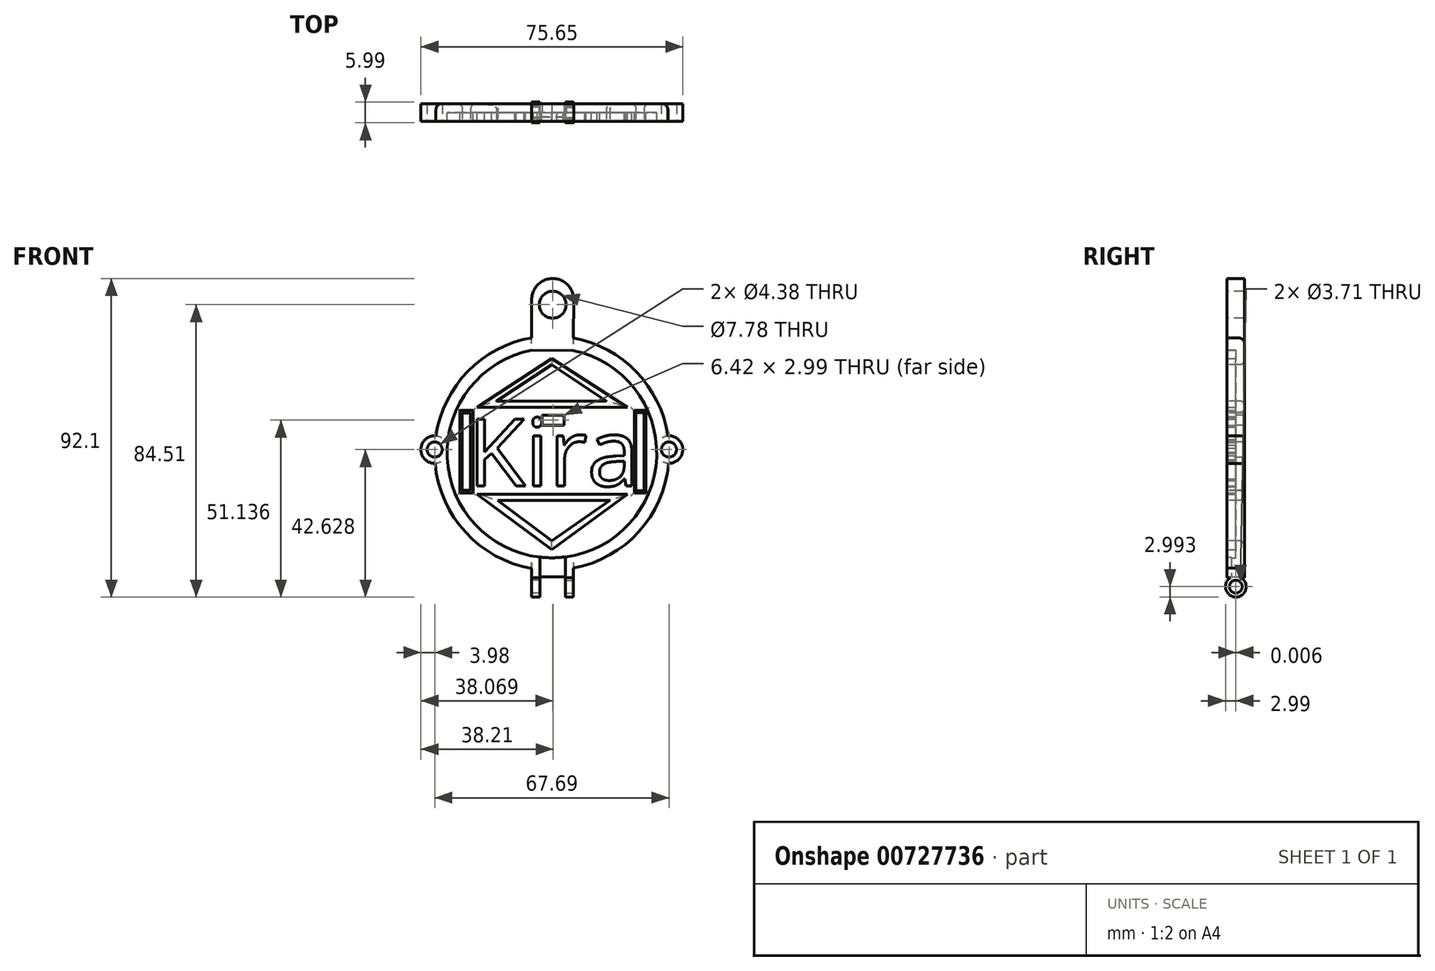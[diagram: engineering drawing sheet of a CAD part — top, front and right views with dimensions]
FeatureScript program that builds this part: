
annotation { "Feature Type Name" : "Feature", "Feature Type Description" : "" }
export const myFeature = defineFeature(function(context is Context, id is Id, definition is map)
    precondition{}
    {
        {
            var Q0;
            Q0=qCreatedBy(makeId("Front.planeOp"),FACE);
            var sketch = newSketch(context, id + "F0", { "sketchPlane" : qUnion([Q0])});
            skCircle(sketch, "E0", {"center": v(0, 0) * mm, "radius": 30.29 * mm});
            skCircle(sketch, "E1", {"center": v(0, 0) * mm, "radius": 33.87 * mm});
            skSolve(sketch);
        }
        {
            var Q0;
            Q0 = qSketchRegion(id + "F0", true);
            extrude(context, id + "F1", {"entities" : qUnion([Q0]), "depth" : 5.08 * mm, "offsetDistance" : 25 * mm});
        }
        {
            var Q0;
            Q0=makeQuery(id+"F1.opExtrude","CAP_FACE",FACE,{"disambiguationData":[OSD([sQuery(id+"F0.wireOp",EDGE,"E0"),sQuery(id+"F0.wireOp",EDGE,"E1")])],"isStart":true});
            var sketch = newSketch(context, id + "F2", { "sketchPlane" : qUnion([Q0])});
            skCircle(sketch, "E2", {"center": v(0, 0) * mm, "radius": 33.85 * mm});
            skSolve(sketch);
        }
        {
            var Q0;
            Q0 = qSketchRegion(id + "F2", true);
            extrude(context, id + "F3", {"entities" : qUnion([Q0]), "operationType" : NewBodyOperationType.ADD, "oppositeDirection" : true, "depth" : 2.54 * mm, "offsetDistance" : 25 * mm});
        }
        {
            var Q0;
            Q0=makeQuery(id+"F1.opExtrude","CAP_FACE",FACE,{"disambiguationData":[OSD([sQuery(id+"F0.wireOp",EDGE,"E0"),sQuery(id+"F0.wireOp",EDGE,"E1")])],"isStart":false});
            var sketch = newSketch(context, id + "F4", { "sketchPlane" : qUnion([Q0])});
            skLineSegment(sketch, "E3", {"start": v(-5.84, 29.72) * mm, "end": v(-5.84, 51.23) * mm});
            skLineSegment(sketch, "E4", {"start": v(-5.84, 51.23) * mm, "end": v(6.2, 51.23) * mm});
            skLineSegment(sketch, "E5", {"start": v(6.2, 51.23) * mm, "end": v(6.2, 29.64) * mm});
            skLineSegment(sketch, "E6", {"start": v(6.2, 29.64) * mm, "end": v(-5.84, 29.72) * mm});
            skSolve(sketch);
        }
        {
            var Q0;
            Q0 = qSketchRegion(id + "F4", true);
            extrude(context, id + "F5", {"entities" : qUnion([Q0]), "operationType" : NewBodyOperationType.REMOVE, "oppositeDirection" : true, "depth" : 25 * mm, "offsetDistance" : 25 * mm});
        }
        {
            var Q0;
            Q0=makeQuery(id+"F3.boolean.opBoolean","MERGE",FACE,{"derivedFrom":[makeQuery(id+"F1.opExtrude","CAP_FACE",FACE,{"disambiguationData":[OSD([sQuery(id+"F0.wireOp",EDGE,"E0"),sQuery(id+"F0.wireOp",EDGE,"E1")])],"isStart":true}),makeQuery(id+"F3.opExtrude","CAP_FACE",FACE,{"disambiguationData":[OSD([sQuery(id+"F2.wireOp",EDGE,"E2")])],"isStart":true})]});
            var sketch = newSketch(context, id + "F6", { "sketchPlane" : qUnion([Q0])});
            skLineSegment(sketch, "E7", {"start": v(-6.2, 29.64) * mm, "end": v(-6.3, 44.37) * mm});
            skLineSegment(sketch, "E8", {"start": v(5.84, 44.37) * mm, "end": v(5.84, 29.72) * mm});
            skLineSegment(sketch, "E9", {"start": v(5.84, 29.72) * mm, "end": v(-6.2, 29.64) * mm});
            skArc(sketch, "E10", {"start": v(-6.3, 44.37) * mm, "mid": v(-0.23, 50.48) * mm, "end": v(5.84, 44.37) * mm});
            skSolve(sketch);
        }
        {
            var Q0;
            Q0 = qSketchRegion(id + "F6", true);
            extrude(context, id + "F7", {"entities" : qUnion([Q0]), "operationType" : NewBodyOperationType.ADD, "oppositeDirection" : true, "depth" : 5.08 * mm, "offsetDistance" : 25 * mm});
        }
        {
            var Q0;
            Q0=makeQuery(id+"F7.boolean.opBoolean","MERGE",FACE,{"derivedFrom":[makeQuery(id+"F1.opExtrude","CAP_FACE",FACE,{"disambiguationData":[OSD([sQuery(id+"F0.wireOp",EDGE,"E0"),sQuery(id+"F0.wireOp",EDGE,"E1")])],"isStart":false}),makeQuery(id+"F7.opExtrude","CAP_FACE",FACE,{"disambiguationData":[OSD([sQuery(id+"F6.wireOp",EDGE,"E7"),sQuery(id+"F6.wireOp",EDGE,"E8"),sQuery(id+"F6.wireOp",EDGE,"E9"),sQuery(id+"F6.wireOp",EDGE,"E10")])],"isStart":false})]});
            var sketch = newSketch(context, id + "F8", { "sketchPlane" : qUnion([Q0])});
            skCircle(sketch, "E11", {"center": v(0.23, 42.89) * mm, "radius": 3.9 * mm});
            skPoint(sketch, "E11.centerSnap0", {"position": v(0.23, 50.48) * mm});
            skSolve(sketch);
        }
        {
            var Q0;
            Q0 = qSketchRegion(id + "F8", true);
            extrude(context, id + "F9", {"entities" : qUnion([Q0]), "operationType" : NewBodyOperationType.REMOVE, "oppositeDirection" : true, "depth" : 25 * mm, "offsetDistance" : 25 * mm});
        }
        {
            var Q0;
            Q0=makeQuery(id+"F3.opExtrude","CAP_FACE",FACE,{"disambiguationData":[OSD([sQuery(id+"F2.wireOp",EDGE,"E2")])],"isStart":false});
            var sketch = newSketch(context, id + "F10", { "sketchPlane" : qUnion([Q0])});
            skText(sketch, "E12", { "text": "Kira", "fontName": "OpenSans-Regular.ttf"});
            const initialGuessF10  = {"E12": [-0.02431, -0.00948, 1, 0, 0.0195]};
            skSetInitialGuess(sketch, initialGuessF10);
            skSolve(sketch);
        }
        {
            var Q0;
            Q0 = qSketchRegion(id + "F10", true);
            extrude(context, id + "F11", {"entities" : qUnion([Q0]), "operationType" : NewBodyOperationType.ADD, "depth" : 2.54 * mm, "offsetDistance" : 25 * mm});
        }
        {
            var Q0;
            Q0=makeQuery(id+"F11.boolean.opBoolean","SPLIT",FACE,{"disambiguationData":[TD([makeQuery(id+"F1.opExtrude","SWEPT_FACE",FACE,{"disambiguationData":[OSD([sQuery(id+"F0.wireOp",EDGE,"E0")])]})])],"derivedFrom":makeQuery(id+"F3.opExtrude","CAP_FACE",FACE,{"disambiguationData":[OSD([sQuery(id+"F2.wireOp",EDGE,"E2")])],"isStart":false})});
            var sketch = newSketch(context, id + "F12", { "sketchPlane" : qUnion([Q0])});
            skLineSegment(sketch, "E13", {"start": v(-21.66, 13.22) * mm, "end": v(21.85, 13.22) * mm});
            skLineSegment(sketch, "E14", {"start": v(-21.66, 13.22) * mm, "end": v(0, 27.38) * mm});
            skLineSegment(sketch, "E15", {"start": v(0, 27.38) * mm, "end": v(21.85, 13.22) * mm});
            skPoint(sketch, "E16", {"position": v(0.18, 29.68) * mm});
            skLineSegment(sketch, "E17", {"start": v(-21.66, -11.88) * mm, "end": v(21.85, -11.88) * mm});
            skLineSegment(sketch, "E18", {"start": v(21.85, -11.88) * mm, "end": v(0, -27.93) * mm});
            skLineSegment(sketch, "E19", {"start": v(0, -27.93) * mm, "end": v(-21.66, -11.88) * mm});
            skSolve(sketch);
        }
        {
            var Q0;
            Q0 = qSketchRegion(id + "F12", true);
            extrude(context, id + "F13", {"entities" : qUnion([Q0]), "operationType" : NewBodyOperationType.ADD, "depth" : 2.54 * mm, "offsetDistance" : 25 * mm});
        }
        {
            var Q0;
            Q0=makeQuery(id+"F13.opExtrude","CAP_FACE",FACE,{"disambiguationData":[OSD([sQuery(id+"F12.wireOp",EDGE,"E13"),sQuery(id+"F12.wireOp",EDGE,"E14"),sQuery(id+"F12.wireOp",EDGE,"E15")])],"isStart":false});
            var sketch = newSketch(context, id + "F14", { "sketchPlane" : qUnion([Q0])});
            skLineSegment(sketch, "E20", {"start": v(0, 25.5) * mm, "end": v(-15.97, 15.06) * mm});
            skLineSegment(sketch, "E21", {"start": v(-15.97, 15.06) * mm, "end": v(15.7, 15.06) * mm});
            skLineSegment(sketch, "E22", {"start": v(15.7, 15.06) * mm, "end": v(0, 25.5) * mm});
            skLineSegment(sketch, "E23", {"start": v(0, -25.41) * mm, "end": v(16.76, -13.65) * mm});
            skLineSegment(sketch, "E24", {"start": v(16.76, -13.65) * mm, "end": v(-15.67, -13.65) * mm});
            skLineSegment(sketch, "E25", {"start": v(-15.67, -13.65) * mm, "end": v(0, -25.41) * mm});
            skSolve(sketch);
        }
        {
            var Q0;
            Q0 = qSketchRegion(id + "F14", true);
            extrude(context, id + "F15", {"entities" : qUnion([Q0]), "operationType" : NewBodyOperationType.REMOVE, "oppositeDirection" : true, "depth" : 25 * mm, "offsetDistance" : 25 * mm});
        }
        {
            var Q0;
            Q0=makeQuery(id+"F11.boolean.opBoolean","SPLIT",FACE,{"disambiguationData":[TD([makeQuery(id+"F1.opExtrude","SWEPT_FACE",FACE,{"disambiguationData":[OSD([sQuery(id+"F0.wireOp",EDGE,"E0")])]})])],"derivedFrom":makeQuery(id+"F3.opExtrude","CAP_FACE",FACE,{"disambiguationData":[OSD([sQuery(id+"F2.wireOp",EDGE,"E2")])],"isStart":false})});
            var sketch = newSketch(context, id + "F16", { "sketchPlane" : qUnion([Q0])});
            skLineSegment(sketch, "E26.bottom", {"start": v(-26.62, 12.34) * mm, "end": v(-22.72, 12.34) * mm});
            skLineSegment(sketch, "E26.top", {"start": v(-26.62, -11.48) * mm, "end": v(-22.72, -11.48) * mm});
            skLineSegment(sketch, "E26.left", {"start": v(-26.62, 12.34) * mm, "end": v(-26.62, -11.48) * mm});
            skLineSegment(sketch, "E26.right", {"start": v(-22.72, 12.34) * mm, "end": v(-22.72, -11.48) * mm});
            skLineSegment(sketch, "E27.bottom", {"start": v(23.79, 12.34) * mm, "end": v(27.12, 12.34) * mm});
            skLineSegment(sketch, "E27.top", {"start": v(23.79, -11.48) * mm, "end": v(27.12, -11.48) * mm});
            skLineSegment(sketch, "E27.left", {"start": v(23.79, 12.34) * mm, "end": v(23.79, -11.48) * mm});
            skLineSegment(sketch, "E27.right", {"start": v(27.12, 12.34) * mm, "end": v(27.12, -11.48) * mm});
            skSolve(sketch);
        }
        {
            var Q0;
            Q0 = qSketchRegion(id + "F16", true);
            extrude(context, id + "F17", {"entities" : qUnion([Q0]), "operationType" : NewBodyOperationType.ADD, "depth" : 2.54 * mm, "offsetDistance" : 25 * mm});
        }
        {
            var Q0;
            Q0=makeQuery(id+"F17.opExtrude","CAP_FACE",FACE,{"disambiguationData":[OSD([sQuery(id+"F16.wireOp",EDGE,"E26.bottom"),sQuery(id+"F16.wireOp",EDGE,"E26.top"),sQuery(id+"F16.wireOp",EDGE,"E26.left"),sQuery(id+"F16.wireOp",EDGE,"E26.right")])],"isStart":false});
            var sketch = newSketch(context, id + "F18", { "sketchPlane" : qUnion([Q0])});
            skLineSegment(sketch, "E28", {"start": v(-25.9, 11.59) * mm, "end": v(-23.46, 11.59) * mm});
            skLineSegment(sketch, "E29", {"start": v(-23.46, 11.59) * mm, "end": v(-23.46, -10.73) * mm});
            skLineSegment(sketch, "E30", {"start": v(-25.9, 11.59) * mm, "end": v(-25.9, -10.73) * mm});
            skLineSegment(sketch, "E31", {"start": v(-25.9, -10.73) * mm, "end": v(-23.46, -10.73) * mm});
            skSolve(sketch);
        }
        {
            var Q0;
            Q0 = qSketchRegion(id + "F18", true);
            extrude(context, id + "F19", {"entities" : qUnion([Q0]), "operationType" : NewBodyOperationType.REMOVE, "oppositeDirection" : true, "depth" : 25 * mm, "offsetDistance" : 25 * mm});
        }
        {
            var Q0;
            Q0=makeQuery(id+"F17.opExtrude","CAP_FACE",FACE,{"disambiguationData":[OSD([sQuery(id+"F16.wireOp",EDGE,"E27.bottom"),sQuery(id+"F16.wireOp",EDGE,"E27.top"),sQuery(id+"F16.wireOp",EDGE,"E27.left"),sQuery(id+"F16.wireOp",EDGE,"E27.right")])],"isStart":false});
            var sketch = newSketch(context, id + "F20", { "sketchPlane" : qUnion([Q0])});
            skLineSegment(sketch, "E32", {"start": v(24.3, 11.73) * mm, "end": v(26.65, 11.73) * mm});
            skLineSegment(sketch, "E33", {"start": v(26.65, 11.73) * mm, "end": v(26.65, -10.9) * mm});
            skLineSegment(sketch, "E34", {"start": v(26.65, -10.9) * mm, "end": v(24.3, -10.9) * mm});
            skLineSegment(sketch, "E35", {"start": v(24.3, -10.9) * mm, "end": v(24.3, 11.73) * mm});
            skSolve(sketch);
        }
        {
            var Q0;
            Q0 = qSketchRegion(id + "F20", true);
            extrude(context, id + "F21", {"entities" : qUnion([Q0]), "operationType" : NewBodyOperationType.REMOVE, "oppositeDirection" : true, "depth" : 25 * mm, "offsetDistance" : 25 * mm});
        }
        {
            var Q0;
            Q0=makeQuery(id+"F7.boolean.opBoolean","MERGE",FACE,{"derivedFrom":[makeQuery(id+"F1.opExtrude","CAP_FACE",FACE,{"disambiguationData":[OSD([sQuery(id+"F0.wireOp",EDGE,"E0"),sQuery(id+"F0.wireOp",EDGE,"E1")])],"isStart":false}),makeQuery(id+"F7.opExtrude","CAP_FACE",FACE,{"disambiguationData":[OSD([sQuery(id+"F6.wireOp",EDGE,"E7"),sQuery(id+"F6.wireOp",EDGE,"E8"),sQuery(id+"F6.wireOp",EDGE,"E9"),sQuery(id+"F6.wireOp",EDGE,"E10")])],"isStart":false})]});
            var sketch = newSketch(context, id + "F22", { "sketchPlane" : qUnion([Q0])});
            skArc(sketch, "E36", {"start": v(-33.5, 4.98) * mm, "mid": v(-37.84, 1.13) * mm, "end": v(-33.73, -2.97) * mm});
            skArc(sketch, "E37", {"start": v(33.73, -2.97) * mm, "mid": v(37.8, 1.13) * mm, "end": v(33.5, 4.98) * mm});
            skLineSegment(sketch, "E38", {"start": v(-33.5, 4.98) * mm, "end": v(-33.73, -2.97) * mm});
            skLineSegment(sketch, "E39", {"start": v(33.73, -2.97) * mm, "end": v(33.5, 4.98) * mm});
            skSolve(sketch);
        }
        {
            var Q0;
            Q0 = qSketchRegion(id + "F22", true);
            extrude(context, id + "F23", {"entities" : qUnion([Q0]), "operationType" : NewBodyOperationType.ADD, "oppositeDirection" : true, "depth" : 5.08 * mm, "offsetDistance" : 25 * mm});
        }
        {
            var Q0;
            Q0=makeQuery(id+"F23.boolean.opBoolean","MERGE",FACE,{"derivedFrom":[makeQuery(id+"F7.boolean.opBoolean","MERGE",FACE,{"derivedFrom":[makeQuery(id+"F1.opExtrude","CAP_FACE",FACE,{"disambiguationData":[OSD([sQuery(id+"F0.wireOp",EDGE,"E0"),sQuery(id+"F0.wireOp",EDGE,"E1")])],"isStart":false}),makeQuery(id+"F7.opExtrude","CAP_FACE",FACE,{"disambiguationData":[OSD([sQuery(id+"F6.wireOp",EDGE,"E7"),sQuery(id+"F6.wireOp",EDGE,"E8"),sQuery(id+"F6.wireOp",EDGE,"E9"),sQuery(id+"F6.wireOp",EDGE,"E10")])],"isStart":false})]}),makeQuery(id+"F23.opExtrude","CAP_FACE",FACE,{"disambiguationData":[OSD([sQuery(id+"F22.wireOp",EDGE,"E36"),sQuery(id+"F22.wireOp",EDGE,"E38")])],"isStart":true}),makeQuery(id+"F23.opExtrude","CAP_FACE",FACE,{"disambiguationData":[OSD([sQuery(id+"F22.wireOp",EDGE,"E37"),sQuery(id+"F22.wireOp",EDGE,"E39")])],"isStart":true})]});
            var sketch = newSketch(context, id + "F24", { "sketchPlane" : qUnion([Q0])});
            skPoint(sketch, "E40.centerSnap0", {"position": v(-37.84, 1.13) * mm});
            skCircle(sketch, "E41", {"center": v(-33.86, 1) * mm, "radius": 2.2 * mm});
            skCircle(sketch, "E42", {"center": v(33.83, 1) * mm, "radius": 2.19 * mm});
            skSolve(sketch);
        }
        {
            var Q0;
            Q0 = qSketchRegion(id + "F24", true);
            extrude(context, id + "F25", {"entities" : qUnion([Q0]), "operationType" : NewBodyOperationType.REMOVE, "oppositeDirection" : true, "depth" : 25 * mm, "offsetDistance" : 25 * mm});
        }
        {
            var Q0;
            Q0 = qSketchRegion(id + "F24", true);
            extrude(context, id + "F26", {"entities" : qUnion([Q0]), "operationType" : NewBodyOperationType.REMOVE, "oppositeDirection" : true, "depth" : 25 * mm, "offsetDistance" : 25 * mm});
        }
        {
            var Q0;
            Q0=makeQuery(id+"F23.boolean.opBoolean","MERGE",FACE,{"derivedFrom":[makeQuery(id+"F7.boolean.opBoolean","MERGE",FACE,{"derivedFrom":[makeQuery(id+"F1.opExtrude","CAP_FACE",FACE,{"disambiguationData":[OSD([sQuery(id+"F0.wireOp",EDGE,"E0"),sQuery(id+"F0.wireOp",EDGE,"E1")])],"isStart":false}),makeQuery(id+"F7.opExtrude","CAP_FACE",FACE,{"disambiguationData":[OSD([sQuery(id+"F6.wireOp",EDGE,"E7"),sQuery(id+"F6.wireOp",EDGE,"E8"),sQuery(id+"F6.wireOp",EDGE,"E9"),sQuery(id+"F6.wireOp",EDGE,"E10")])],"isStart":false})]}),makeQuery(id+"F23.opExtrude","CAP_FACE",FACE,{"disambiguationData":[OSD([sQuery(id+"F22.wireOp",EDGE,"E36"),sQuery(id+"F22.wireOp",EDGE,"E38")])],"isStart":true}),makeQuery(id+"F23.opExtrude","CAP_FACE",FACE,{"disambiguationData":[OSD([sQuery(id+"F22.wireOp",EDGE,"E37"),sQuery(id+"F22.wireOp",EDGE,"E39")])],"isStart":true})]});
            var sketch = newSketch(context, id + "F27", { "sketchPlane" : qUnion([Q0])});
            skPoint(sketch, "E43", {"position": v(-5.84, -33.36) * mm});
            skLineSegment(sketch, "E44", {"start": v(6.23, -33.29) * mm, "end": v(6.23, -36.03) * mm});
            skLineSegment(sketch, "E45", {"start": v(6.23, -36.03) * mm, "end": v(-5.84, -36.03) * mm});
            skLineSegment(sketch, "E46", {"start": v(-5.84, -33.36) * mm, "end": v(6.23, -33.29) * mm});
            skLineSegment(sketch, "E47", {"start": v(-5.84, -33.36) * mm, "end": v(-5.84, -36.03) * mm});
            skSolve(sketch);
        }
        {
            var Q0;
            Q0 = qSketchRegion(id + "F27", true);
            extrude(context, id + "F28", {"entities" : qUnion([Q0]), "operationType" : NewBodyOperationType.ADD, "oppositeDirection" : true, "depth" : 5.08 * mm, "offsetDistance" : 25 * mm});
        }
        {
            var Q0;
            Q0=makeQuery(id+"F28.opExtrude","SWEPT_FACE",FACE,{"disambiguationData":[OSD([sQuery(id+"F27.wireOp",EDGE,"E47")])]});
            var sketch = newSketch(context, id + "F29", { "sketchPlane" : qUnion([Q0])});
            skCircle(sketch, "E48", {"center": v(2.54, -38.63) * mm, "radius": 3 * mm});
            skPoint(sketch, "E48.centerSnap0", {"position": v(2.54, -36.03) * mm});
            skCircle(sketch, "E49", {"center": v(2.54, -38.63) * mm, "radius": 1.86 * mm});
            skSolve(sketch);
        }
        {
            var Q0;
            Q0 = qSketchRegion(id + "F29", true);
            extrude(context, id + "F30", {"entities" : qUnion([Q0]), "operationType" : NewBodyOperationType.ADD, "oppositeDirection" : true, "depth" : 2.36 * mm, "offsetDistance" : 25 * mm});
        }
        {
            var Q0;
            Q0=makeQuery(id+"F28.opExtrude","SWEPT_FACE",FACE,{"disambiguationData":[OSD([sQuery(id+"F27.wireOp",EDGE,"E44")])]});
            var sketch = newSketch(context, id + "F31", { "sketchPlane" : qUnion([Q0])});
            skCircle(sketch, "E50", {"center": v(-2.53, -38.63) * mm, "radius": 3 * mm});
            skCircle(sketch, "E51", {"center": v(-2.53, -38.63) * mm, "radius": 1.86 * mm});
            skSolve(sketch);
        }
        {
            var Q0;
            Q0 = qSketchRegion(id + "F31", true);
            extrude(context, id + "F32", {"entities" : qUnion([Q0]), "operationType" : NewBodyOperationType.ADD, "oppositeDirection" : true, "depth" : 2.28 * mm, "offsetDistance" : 25 * mm});
        }
        {
            var Q0;
            Q0=makeQuery(id+"F11.boolean.opBoolean","SPLIT",FACE,{"disambiguationData":[TD([makeQuery(id+"F1.opExtrude","SWEPT_FACE",FACE,{"disambiguationData":[OSD([sQuery(id+"F0.wireOp",EDGE,"E0")])]})])],"derivedFrom":makeQuery(id+"F3.opExtrude","CAP_FACE",FACE,{"disambiguationData":[OSD([sQuery(id+"F2.wireOp",EDGE,"E2")])],"isStart":false})});
            var sketch = newSketch(context, id + "F33", { "sketchPlane" : qUnion([Q0])});
            skPoint(sketch, "E52.startSnap0", {"position": v(-24.67, 12.34) * mm});
            skLineSegment(sketch, "E53", {"start": v(-2.84, 8.08) * mm, "end": v(3.58, 8.02) * mm});
            skLineSegment(sketch, "E54", {"start": v(-2.84, 11.01) * mm, "end": v(3.58, 11.01) * mm});
            skLineSegment(sketch, "E55", {"start": v(3.58, 11.01) * mm, "end": v(3.58, 8.02) * mm});
            skLineSegment(sketch, "E56", {"start": v(-2.84, 11.01) * mm, "end": v(-2.84, 8.08) * mm});
            skSolve(sketch);
        }
        {
            var Q0;
            Q0 = qSketchRegion(id + "F33", true);
            extrude(context, id + "F34", {"entities" : qUnion([Q0]), "operationType" : NewBodyOperationType.REMOVE, "oppositeDirection" : true, "depth" : 25 * mm, "offsetDistance" : 25 * mm});
        }
        {
            var Q0;
            Q0=makeQuery(id+"F28.opExtrude","SWEPT_FACE",FACE,{"disambiguationData":[OSD([sQuery(id+"F27.wireOp",EDGE,"E45")])]});
            var sketch = newSketch(context, id + "F35", { "sketchPlane" : qUnion([Q0])});
            skLineSegment(sketch, "E57", {"start": v(-3.47, 5.08) * mm, "end": v(-3.47, 0) * mm});
            skLineSegment(sketch, "E58", {"start": v(-3.47, 0) * mm, "end": v(3.95, 0) * mm});
            skLineSegment(sketch, "E59", {"start": v(3.95, 0) * mm, "end": v(3.95, 5.08) * mm});
            skLineSegment(sketch, "E60", {"start": v(3.95, 5.08) * mm, "end": v(-3.47, 5.08) * mm});
            skSolve(sketch);
        }
        {
            var Q0;
            Q0 = qSketchRegion(id + "F35", true);
            extrude(context, id + "F36", {"entities" : qUnion([Q0]), "operationType" : NewBodyOperationType.REMOVE, "oppositeDirection" : true, "depth" : 0.26 * mm, "offsetDistance" : 25 * mm});
        }
        {
            var Q0;
            Q0=makeQuery(id+"F36.boolean.opBoolean","COPY",FACE,{"derivedFrom":makeQuery(id+"F36.opExtrude","CAP_FACE",FACE,{"disambiguationData":[OSD([sQuery(id+"F35.wireOp",EDGE,"E57"),sQuery(id+"F35.wireOp",EDGE,"E58"),sQuery(id+"F35.wireOp",EDGE,"E59"),sQuery(id+"F35.wireOp",EDGE,"E60")])],"isStart":false})});
            var sketch = newSketch(context, id + "F37", { "sketchPlane" : qUnion([Q0])});
            skLineSegment(sketch, "E61", {"start": v(-3.47, 5.08) * mm, "end": v(3.95, 5.08) * mm});
            skLineSegment(sketch, "E62", {"start": v(-3.47, 3.83) * mm, "end": v(3.95, 3.83) * mm});
            skLineSegment(sketch, "E63", {"start": v(3.95, 3.83) * mm, "end": v(3.95, 5.08) * mm});
            skLineSegment(sketch, "E64", {"start": v(-3.47, 3.83) * mm, "end": v(-3.47, 5.08) * mm});
            skSolve(sketch);
        }
        {
            var Q0;
            Q0 = qSketchRegion(id + "F37", true);
            extrude(context, id + "F38", {"entities" : qUnion([Q0]), "operationType" : NewBodyOperationType.REMOVE, "oppositeDirection" : true, "depth" : 6.9 * mm, "offsetDistance" : 25 * mm});
        }
        {
            var Q0;
            {var subQ0=sQuery(id+"F6.wireOp",EDGE,"E8");var subQ1=sQuery(id+"F0.wireOp",EDGE,"E1");var subQ2=sQuery(id+"F22.wireOp",EDGE,"E36");Q0=makeQuery(id+"F23.boolean.opBoolean","SPLIT",EDGE,{"disambiguationData":[TD([makeQuery(id+"F1.opExtrude","CAP_FACE",FACE,{"disambiguationData":[OSD([sQuery(id+"F0.wireOp",EDGE,"E0"),subQ1])],"isStart":true}),makeQuery(id+"F1.opExtrude","SWEPT_FACE",FACE,{"disambiguationData":[OSD([subQ1])]}),makeQuery(id+"F3.opExtrude","CAP_FACE",FACE,{"disambiguationData":[OSD([sQuery(id+"F2.wireOp",EDGE,"E2")])],"isStart":true}),makeQuery(id+"F7.opExtrude","CAP_FACE",FACE,{"disambiguationData":[OSD([sQuery(id+"F6.wireOp",EDGE,"E7"),subQ0,sQuery(id+"F6.wireOp",EDGE,"E9"),sQuery(id+"F6.wireOp",EDGE,"E10")])],"isStart":true}),makeQuery(id+"F7.opExtrude","SWEPT_FACE",FACE,{"disambiguationData":[OSD([subQ0])]}),makeQuery(id+"F23.opExtrude","SWEPT_FACE",FACE,{"disambiguationData":[OSD([subQ2])]}),makeQuery(id+"F23.opExtrude","CAP_FACE",FACE,{"disambiguationData":[OSD([subQ2,sQuery(id+"F22.wireOp",EDGE,"E38")])],"isStart":false}),makeQuery(id+"F23.opExtrude","CAP_FACE",FACE,{"disambiguationData":[OSD([sQuery(id+"F22.wireOp",EDGE,"E37"),sQuery(id+"F22.wireOp",EDGE,"E39")])],"isStart":false})])],"derivedFrom":makeQuery(id+"F1.opExtrude","CAP_EDGE",EDGE,{"disambiguationData":[OSD([subQ1])],"isStart":true})});}
            var Q1;
            {var subQ0=makeQuery(id+"F7.opExtrude","CAP_FACE",FACE,{"disambiguationData":[OSD([sQuery(id+"F6.wireOp",EDGE,"E7"),sQuery(id+"F6.wireOp",EDGE,"E8"),sQuery(id+"F6.wireOp",EDGE,"E9"),sQuery(id+"F6.wireOp",EDGE,"E10")])],"isStart":true});var subQ1=sQuery(id+"F0.wireOp",EDGE,"E1");var subQ2=makeQuery(id+"F1.opExtrude","CAP_FACE",FACE,{"disambiguationData":[OSD([sQuery(id+"F0.wireOp",EDGE,"E0"),subQ1])],"isStart":true});var subQ3=makeQuery(id+"F3.opExtrude","CAP_FACE",FACE,{"disambiguationData":[OSD([sQuery(id+"F2.wireOp",EDGE,"E2")])],"isStart":true});var subQ4=sQuery(id+"F22.wireOp",EDGE,"E36");var subQ5=makeQuery(id+"F23.opExtrude","CAP_FACE",FACE,{"disambiguationData":[OSD([subQ4,sQuery(id+"F22.wireOp",EDGE,"E38")])],"isStart":false});var subQ6=makeQuery(id+"F1.opExtrude","SWEPT_FACE",FACE,{"disambiguationData":[OSD([subQ1])]});var subQ7=sQuery(id+"F22.wireOp",EDGE,"E37");var subQ8=makeQuery(id+"F23.opExtrude","SWEPT_FACE",FACE,{"disambiguationData":[OSD([subQ7])]});var subQ9=makeQuery(id+"F23.opExtrude","CAP_FACE",FACE,{"disambiguationData":[OSD([subQ7,sQuery(id+"F22.wireOp",EDGE,"E39")])],"isStart":false});Q1=makeQuery(id+"F28.boolean.opBoolean","SPLIT",EDGE,{"disambiguationData":[TD([subQ8])],"derivedFrom":makeQuery(id+"F23.boolean.opBoolean","SPLIT",EDGE,{"disambiguationData":[TD([subQ2,subQ6,subQ3,subQ0,makeQuery(id+"F23.opExtrude","SWEPT_FACE",FACE,{"disambiguationData":[OSD([subQ4])]}),subQ5,subQ8,subQ9])],"derivedFrom":makeQuery(id+"F1.opExtrude","CAP_EDGE",EDGE,{"disambiguationData":[OSD([subQ1])],"isStart":true})})});}
            var Q2;
            {var subQ0=makeQuery(id+"F7.opExtrude","CAP_FACE",FACE,{"disambiguationData":[OSD([sQuery(id+"F6.wireOp",EDGE,"E7"),sQuery(id+"F6.wireOp",EDGE,"E8"),sQuery(id+"F6.wireOp",EDGE,"E9"),sQuery(id+"F6.wireOp",EDGE,"E10")])],"isStart":true});var subQ1=sQuery(id+"F0.wireOp",EDGE,"E1");var subQ2=makeQuery(id+"F1.opExtrude","CAP_FACE",FACE,{"disambiguationData":[OSD([sQuery(id+"F0.wireOp",EDGE,"E0"),subQ1])],"isStart":true});var subQ3=makeQuery(id+"F3.opExtrude","CAP_FACE",FACE,{"disambiguationData":[OSD([sQuery(id+"F2.wireOp",EDGE,"E2")])],"isStart":true});var subQ4=sQuery(id+"F22.wireOp",EDGE,"E36");var subQ5=makeQuery(id+"F23.opExtrude","CAP_FACE",FACE,{"disambiguationData":[OSD([subQ4,sQuery(id+"F22.wireOp",EDGE,"E38")])],"isStart":false});var subQ6=makeQuery(id+"F1.opExtrude","SWEPT_FACE",FACE,{"disambiguationData":[OSD([subQ1])]});var subQ7=makeQuery(id+"F23.opExtrude","SWEPT_FACE",FACE,{"disambiguationData":[OSD([subQ4])]});var subQ8=sQuery(id+"F22.wireOp",EDGE,"E37");var subQ9=makeQuery(id+"F23.opExtrude","CAP_FACE",FACE,{"disambiguationData":[OSD([subQ8,sQuery(id+"F22.wireOp",EDGE,"E39")])],"isStart":false});Q2=makeQuery(id+"F28.boolean.opBoolean","SPLIT",EDGE,{"disambiguationData":[TD([subQ7])],"derivedFrom":makeQuery(id+"F23.boolean.opBoolean","SPLIT",EDGE,{"disambiguationData":[TD([subQ2,subQ6,subQ3,subQ0,subQ7,subQ5,makeQuery(id+"F23.opExtrude","SWEPT_FACE",FACE,{"disambiguationData":[OSD([subQ8])]}),subQ9])],"derivedFrom":makeQuery(id+"F1.opExtrude","CAP_EDGE",EDGE,{"disambiguationData":[OSD([subQ1])],"isStart":true})})});}
            var Q3;
            {var subQ0=sQuery(id+"F0.wireOp",EDGE,"E1");var subQ1=sQuery(id+"F22.wireOp",EDGE,"E37");var subQ2=sQuery(id+"F6.wireOp",EDGE,"E7");Q3=makeQuery(id+"F23.boolean.opBoolean","SPLIT",EDGE,{"disambiguationData":[TD([makeQuery(id+"F1.opExtrude","CAP_FACE",FACE,{"disambiguationData":[OSD([sQuery(id+"F0.wireOp",EDGE,"E0"),subQ0])],"isStart":true}),makeQuery(id+"F1.opExtrude","SWEPT_FACE",FACE,{"disambiguationData":[OSD([subQ0])]}),makeQuery(id+"F3.opExtrude","CAP_FACE",FACE,{"disambiguationData":[OSD([sQuery(id+"F2.wireOp",EDGE,"E2")])],"isStart":true}),makeQuery(id+"F7.opExtrude","SWEPT_FACE",FACE,{"disambiguationData":[OSD([subQ2])]}),makeQuery(id+"F7.opExtrude","CAP_FACE",FACE,{"disambiguationData":[OSD([subQ2,sQuery(id+"F6.wireOp",EDGE,"E8"),sQuery(id+"F6.wireOp",EDGE,"E9"),sQuery(id+"F6.wireOp",EDGE,"E10")])],"isStart":true}),makeQuery(id+"F23.opExtrude","CAP_FACE",FACE,{"disambiguationData":[OSD([sQuery(id+"F22.wireOp",EDGE,"E36"),sQuery(id+"F22.wireOp",EDGE,"E38")])],"isStart":false}),makeQuery(id+"F23.opExtrude","SWEPT_FACE",FACE,{"disambiguationData":[OSD([subQ1])]}),makeQuery(id+"F23.opExtrude","CAP_FACE",FACE,{"disambiguationData":[OSD([subQ1,sQuery(id+"F22.wireOp",EDGE,"E39")])],"isStart":false})])],"derivedFrom":makeQuery(id+"F1.opExtrude","CAP_EDGE",EDGE,{"disambiguationData":[OSD([subQ0])],"isStart":true})});}
            fillet(context, id + "F39", {"entities" : qUnion([Q0, Q1, Q2, Q3]), "radius" : 1.69 * mm, "tangentPropagation" : true, "allowEdgeOverflow" : false});
        }
        {
            var Q0;
            Q0=makeQuery(id+"F15.boolean.opBoolean","INTERSECT",EDGE,{"derivedFrom":[makeQuery(id+"F7.boolean.opBoolean","MERGE",FACE,{"derivedFrom":[makeQuery(id+"F3.boolean.opBoolean","MERGE",FACE,{"derivedFrom":[makeQuery(id+"F1.opExtrude","CAP_FACE",FACE,{"disambiguationData":[OSD([sQuery(id+"F0.wireOp",EDGE,"E0"),sQuery(id+"F0.wireOp",EDGE,"E1")])],"isStart":true}),makeQuery(id+"F3.opExtrude","CAP_FACE",FACE,{"disambiguationData":[OSD([sQuery(id+"F2.wireOp",EDGE,"E2")])],"isStart":true})]}),makeQuery(id+"F7.opExtrude","CAP_FACE",FACE,{"disambiguationData":[OSD([sQuery(id+"F6.wireOp",EDGE,"E7"),sQuery(id+"F6.wireOp",EDGE,"E8"),sQuery(id+"F6.wireOp",EDGE,"E9"),sQuery(id+"F6.wireOp",EDGE,"E10")])],"isStart":true})]}),makeQuery(id+"F15.opExtrude","SWEPT_FACE",FACE,{"disambiguationData":[OSD([sQuery(id+"F14.wireOp",EDGE,"E22")])]})]});
            var Q1;
            Q1=makeQuery(id+"F15.boolean.opBoolean","INTERSECT",EDGE,{"derivedFrom":[makeQuery(id+"F7.boolean.opBoolean","MERGE",FACE,{"derivedFrom":[makeQuery(id+"F3.boolean.opBoolean","MERGE",FACE,{"derivedFrom":[makeQuery(id+"F1.opExtrude","CAP_FACE",FACE,{"disambiguationData":[OSD([sQuery(id+"F0.wireOp",EDGE,"E0"),sQuery(id+"F0.wireOp",EDGE,"E1")])],"isStart":true}),makeQuery(id+"F3.opExtrude","CAP_FACE",FACE,{"disambiguationData":[OSD([sQuery(id+"F2.wireOp",EDGE,"E2")])],"isStart":true})]}),makeQuery(id+"F7.opExtrude","CAP_FACE",FACE,{"disambiguationData":[OSD([sQuery(id+"F6.wireOp",EDGE,"E7"),sQuery(id+"F6.wireOp",EDGE,"E8"),sQuery(id+"F6.wireOp",EDGE,"E9"),sQuery(id+"F6.wireOp",EDGE,"E10")])],"isStart":true})]}),makeQuery(id+"F15.opExtrude","SWEPT_FACE",FACE,{"disambiguationData":[OSD([sQuery(id+"F14.wireOp",EDGE,"E20")])]})]});
            var Q2;
            Q2=makeQuery(id+"F15.boolean.opBoolean","INTERSECT",EDGE,{"derivedFrom":[makeQuery(id+"F7.boolean.opBoolean","MERGE",FACE,{"derivedFrom":[makeQuery(id+"F3.boolean.opBoolean","MERGE",FACE,{"derivedFrom":[makeQuery(id+"F1.opExtrude","CAP_FACE",FACE,{"disambiguationData":[OSD([sQuery(id+"F0.wireOp",EDGE,"E0"),sQuery(id+"F0.wireOp",EDGE,"E1")])],"isStart":true}),makeQuery(id+"F3.opExtrude","CAP_FACE",FACE,{"disambiguationData":[OSD([sQuery(id+"F2.wireOp",EDGE,"E2")])],"isStart":true})]}),makeQuery(id+"F7.opExtrude","CAP_FACE",FACE,{"disambiguationData":[OSD([sQuery(id+"F6.wireOp",EDGE,"E7"),sQuery(id+"F6.wireOp",EDGE,"E8"),sQuery(id+"F6.wireOp",EDGE,"E9"),sQuery(id+"F6.wireOp",EDGE,"E10")])],"isStart":true})]}),makeQuery(id+"F15.opExtrude","SWEPT_FACE",FACE,{"disambiguationData":[OSD([sQuery(id+"F14.wireOp",EDGE,"E21")])]})]});
            var Q3;
            Q3=makeQuery(id+"F21.boolean.opBoolean","INTERSECT",EDGE,{"derivedFrom":[makeQuery(id+"F7.boolean.opBoolean","MERGE",FACE,{"derivedFrom":[makeQuery(id+"F3.boolean.opBoolean","MERGE",FACE,{"derivedFrom":[makeQuery(id+"F1.opExtrude","CAP_FACE",FACE,{"disambiguationData":[OSD([sQuery(id+"F0.wireOp",EDGE,"E0"),sQuery(id+"F0.wireOp",EDGE,"E1")])],"isStart":true}),makeQuery(id+"F3.opExtrude","CAP_FACE",FACE,{"disambiguationData":[OSD([sQuery(id+"F2.wireOp",EDGE,"E2")])],"isStart":true})]}),makeQuery(id+"F7.opExtrude","CAP_FACE",FACE,{"disambiguationData":[OSD([sQuery(id+"F6.wireOp",EDGE,"E7"),sQuery(id+"F6.wireOp",EDGE,"E8"),sQuery(id+"F6.wireOp",EDGE,"E9"),sQuery(id+"F6.wireOp",EDGE,"E10")])],"isStart":true})]}),makeQuery(id+"F21.opExtrude","SWEPT_FACE",FACE,{"disambiguationData":[OSD([sQuery(id+"F20.wireOp",EDGE,"E35")])]})]});
            var Q4;
            Q4=makeQuery(id+"F21.boolean.opBoolean","INTERSECT",EDGE,{"derivedFrom":[makeQuery(id+"F7.boolean.opBoolean","MERGE",FACE,{"derivedFrom":[makeQuery(id+"F3.boolean.opBoolean","MERGE",FACE,{"derivedFrom":[makeQuery(id+"F1.opExtrude","CAP_FACE",FACE,{"disambiguationData":[OSD([sQuery(id+"F0.wireOp",EDGE,"E0"),sQuery(id+"F0.wireOp",EDGE,"E1")])],"isStart":true}),makeQuery(id+"F3.opExtrude","CAP_FACE",FACE,{"disambiguationData":[OSD([sQuery(id+"F2.wireOp",EDGE,"E2")])],"isStart":true})]}),makeQuery(id+"F7.opExtrude","CAP_FACE",FACE,{"disambiguationData":[OSD([sQuery(id+"F6.wireOp",EDGE,"E7"),sQuery(id+"F6.wireOp",EDGE,"E8"),sQuery(id+"F6.wireOp",EDGE,"E9"),sQuery(id+"F6.wireOp",EDGE,"E10")])],"isStart":true})]}),makeQuery(id+"F21.opExtrude","SWEPT_FACE",FACE,{"disambiguationData":[OSD([sQuery(id+"F20.wireOp",EDGE,"E33")])]})]});
            var Q5;
            Q5=makeQuery(id+"F21.boolean.opBoolean","INTERSECT",EDGE,{"derivedFrom":[makeQuery(id+"F7.boolean.opBoolean","MERGE",FACE,{"derivedFrom":[makeQuery(id+"F3.boolean.opBoolean","MERGE",FACE,{"derivedFrom":[makeQuery(id+"F1.opExtrude","CAP_FACE",FACE,{"disambiguationData":[OSD([sQuery(id+"F0.wireOp",EDGE,"E0"),sQuery(id+"F0.wireOp",EDGE,"E1")])],"isStart":true}),makeQuery(id+"F3.opExtrude","CAP_FACE",FACE,{"disambiguationData":[OSD([sQuery(id+"F2.wireOp",EDGE,"E2")])],"isStart":true})]}),makeQuery(id+"F7.opExtrude","CAP_FACE",FACE,{"disambiguationData":[OSD([sQuery(id+"F6.wireOp",EDGE,"E7"),sQuery(id+"F6.wireOp",EDGE,"E8"),sQuery(id+"F6.wireOp",EDGE,"E9"),sQuery(id+"F6.wireOp",EDGE,"E10")])],"isStart":true})]}),makeQuery(id+"F21.opExtrude","SWEPT_FACE",FACE,{"disambiguationData":[OSD([sQuery(id+"F20.wireOp",EDGE,"E32")])]})]});
            var Q6;
            Q6=makeQuery(id+"F21.boolean.opBoolean","INTERSECT",EDGE,{"derivedFrom":[makeQuery(id+"F7.boolean.opBoolean","MERGE",FACE,{"derivedFrom":[makeQuery(id+"F3.boolean.opBoolean","MERGE",FACE,{"derivedFrom":[makeQuery(id+"F1.opExtrude","CAP_FACE",FACE,{"disambiguationData":[OSD([sQuery(id+"F0.wireOp",EDGE,"E0"),sQuery(id+"F0.wireOp",EDGE,"E1")])],"isStart":true}),makeQuery(id+"F3.opExtrude","CAP_FACE",FACE,{"disambiguationData":[OSD([sQuery(id+"F2.wireOp",EDGE,"E2")])],"isStart":true})]}),makeQuery(id+"F7.opExtrude","CAP_FACE",FACE,{"disambiguationData":[OSD([sQuery(id+"F6.wireOp",EDGE,"E7"),sQuery(id+"F6.wireOp",EDGE,"E8"),sQuery(id+"F6.wireOp",EDGE,"E9"),sQuery(id+"F6.wireOp",EDGE,"E10")])],"isStart":true})]}),makeQuery(id+"F21.opExtrude","SWEPT_FACE",FACE,{"disambiguationData":[OSD([sQuery(id+"F20.wireOp",EDGE,"E34")])]})]});
            var Q7;
            Q7=makeQuery(id+"F15.boolean.opBoolean","INTERSECT",EDGE,{"derivedFrom":[makeQuery(id+"F7.boolean.opBoolean","MERGE",FACE,{"derivedFrom":[makeQuery(id+"F3.boolean.opBoolean","MERGE",FACE,{"derivedFrom":[makeQuery(id+"F1.opExtrude","CAP_FACE",FACE,{"disambiguationData":[OSD([sQuery(id+"F0.wireOp",EDGE,"E0"),sQuery(id+"F0.wireOp",EDGE,"E1")])],"isStart":true}),makeQuery(id+"F3.opExtrude","CAP_FACE",FACE,{"disambiguationData":[OSD([sQuery(id+"F2.wireOp",EDGE,"E2")])],"isStart":true})]}),makeQuery(id+"F7.opExtrude","CAP_FACE",FACE,{"disambiguationData":[OSD([sQuery(id+"F6.wireOp",EDGE,"E7"),sQuery(id+"F6.wireOp",EDGE,"E8"),sQuery(id+"F6.wireOp",EDGE,"E9"),sQuery(id+"F6.wireOp",EDGE,"E10")])],"isStart":true})]}),makeQuery(id+"F15.opExtrude","SWEPT_FACE",FACE,{"disambiguationData":[OSD([sQuery(id+"F14.wireOp",EDGE,"E23")])]})]});
            var Q8;
            Q8=makeQuery(id+"F15.boolean.opBoolean","INTERSECT",EDGE,{"derivedFrom":[makeQuery(id+"F7.boolean.opBoolean","MERGE",FACE,{"derivedFrom":[makeQuery(id+"F3.boolean.opBoolean","MERGE",FACE,{"derivedFrom":[makeQuery(id+"F1.opExtrude","CAP_FACE",FACE,{"disambiguationData":[OSD([sQuery(id+"F0.wireOp",EDGE,"E0"),sQuery(id+"F0.wireOp",EDGE,"E1")])],"isStart":true}),makeQuery(id+"F3.opExtrude","CAP_FACE",FACE,{"disambiguationData":[OSD([sQuery(id+"F2.wireOp",EDGE,"E2")])],"isStart":true})]}),makeQuery(id+"F7.opExtrude","CAP_FACE",FACE,{"disambiguationData":[OSD([sQuery(id+"F6.wireOp",EDGE,"E7"),sQuery(id+"F6.wireOp",EDGE,"E8"),sQuery(id+"F6.wireOp",EDGE,"E9"),sQuery(id+"F6.wireOp",EDGE,"E10")])],"isStart":true})]}),makeQuery(id+"F15.opExtrude","SWEPT_FACE",FACE,{"disambiguationData":[OSD([sQuery(id+"F14.wireOp",EDGE,"E24")])]})]});
            var Q9;
            Q9=makeQuery(id+"F15.boolean.opBoolean","INTERSECT",EDGE,{"derivedFrom":[makeQuery(id+"F7.boolean.opBoolean","MERGE",FACE,{"derivedFrom":[makeQuery(id+"F3.boolean.opBoolean","MERGE",FACE,{"derivedFrom":[makeQuery(id+"F1.opExtrude","CAP_FACE",FACE,{"disambiguationData":[OSD([sQuery(id+"F0.wireOp",EDGE,"E0"),sQuery(id+"F0.wireOp",EDGE,"E1")])],"isStart":true}),makeQuery(id+"F3.opExtrude","CAP_FACE",FACE,{"disambiguationData":[OSD([sQuery(id+"F2.wireOp",EDGE,"E2")])],"isStart":true})]}),makeQuery(id+"F7.opExtrude","CAP_FACE",FACE,{"disambiguationData":[OSD([sQuery(id+"F6.wireOp",EDGE,"E7"),sQuery(id+"F6.wireOp",EDGE,"E8"),sQuery(id+"F6.wireOp",EDGE,"E9"),sQuery(id+"F6.wireOp",EDGE,"E10")])],"isStart":true})]}),makeQuery(id+"F15.opExtrude","SWEPT_FACE",FACE,{"disambiguationData":[OSD([sQuery(id+"F14.wireOp",EDGE,"E25")])]})]});
            var Q10;
            Q10=makeQuery(id+"F19.boolean.opBoolean","INTERSECT",EDGE,{"derivedFrom":[makeQuery(id+"F7.boolean.opBoolean","MERGE",FACE,{"derivedFrom":[makeQuery(id+"F3.boolean.opBoolean","MERGE",FACE,{"derivedFrom":[makeQuery(id+"F1.opExtrude","CAP_FACE",FACE,{"disambiguationData":[OSD([sQuery(id+"F0.wireOp",EDGE,"E0"),sQuery(id+"F0.wireOp",EDGE,"E1")])],"isStart":true}),makeQuery(id+"F3.opExtrude","CAP_FACE",FACE,{"disambiguationData":[OSD([sQuery(id+"F2.wireOp",EDGE,"E2")])],"isStart":true})]}),makeQuery(id+"F7.opExtrude","CAP_FACE",FACE,{"disambiguationData":[OSD([sQuery(id+"F6.wireOp",EDGE,"E7"),sQuery(id+"F6.wireOp",EDGE,"E8"),sQuery(id+"F6.wireOp",EDGE,"E9"),sQuery(id+"F6.wireOp",EDGE,"E10")])],"isStart":true})]}),makeQuery(id+"F19.opExtrude","SWEPT_FACE",FACE,{"disambiguationData":[OSD([sQuery(id+"F18.wireOp",EDGE,"E29")])]})]});
            var Q11;
            Q11=makeQuery(id+"F19.boolean.opBoolean","INTERSECT",EDGE,{"derivedFrom":[makeQuery(id+"F7.boolean.opBoolean","MERGE",FACE,{"derivedFrom":[makeQuery(id+"F3.boolean.opBoolean","MERGE",FACE,{"derivedFrom":[makeQuery(id+"F1.opExtrude","CAP_FACE",FACE,{"disambiguationData":[OSD([sQuery(id+"F0.wireOp",EDGE,"E0"),sQuery(id+"F0.wireOp",EDGE,"E1")])],"isStart":true}),makeQuery(id+"F3.opExtrude","CAP_FACE",FACE,{"disambiguationData":[OSD([sQuery(id+"F2.wireOp",EDGE,"E2")])],"isStart":true})]}),makeQuery(id+"F7.opExtrude","CAP_FACE",FACE,{"disambiguationData":[OSD([sQuery(id+"F6.wireOp",EDGE,"E7"),sQuery(id+"F6.wireOp",EDGE,"E8"),sQuery(id+"F6.wireOp",EDGE,"E9"),sQuery(id+"F6.wireOp",EDGE,"E10")])],"isStart":true})]}),makeQuery(id+"F19.opExtrude","SWEPT_FACE",FACE,{"disambiguationData":[OSD([sQuery(id+"F18.wireOp",EDGE,"E30")])]})]});
            var Q12;
            Q12=makeQuery(id+"F19.boolean.opBoolean","INTERSECT",EDGE,{"derivedFrom":[makeQuery(id+"F7.boolean.opBoolean","MERGE",FACE,{"derivedFrom":[makeQuery(id+"F3.boolean.opBoolean","MERGE",FACE,{"derivedFrom":[makeQuery(id+"F1.opExtrude","CAP_FACE",FACE,{"disambiguationData":[OSD([sQuery(id+"F0.wireOp",EDGE,"E0"),sQuery(id+"F0.wireOp",EDGE,"E1")])],"isStart":true}),makeQuery(id+"F3.opExtrude","CAP_FACE",FACE,{"disambiguationData":[OSD([sQuery(id+"F2.wireOp",EDGE,"E2")])],"isStart":true})]}),makeQuery(id+"F7.opExtrude","CAP_FACE",FACE,{"disambiguationData":[OSD([sQuery(id+"F6.wireOp",EDGE,"E7"),sQuery(id+"F6.wireOp",EDGE,"E8"),sQuery(id+"F6.wireOp",EDGE,"E9"),sQuery(id+"F6.wireOp",EDGE,"E10")])],"isStart":true})]}),makeQuery(id+"F19.opExtrude","SWEPT_FACE",FACE,{"disambiguationData":[OSD([sQuery(id+"F18.wireOp",EDGE,"E28")])]})]});
            var Q13;
            Q13=makeQuery(id+"F19.boolean.opBoolean","INTERSECT",EDGE,{"derivedFrom":[makeQuery(id+"F7.boolean.opBoolean","MERGE",FACE,{"derivedFrom":[makeQuery(id+"F3.boolean.opBoolean","MERGE",FACE,{"derivedFrom":[makeQuery(id+"F1.opExtrude","CAP_FACE",FACE,{"disambiguationData":[OSD([sQuery(id+"F0.wireOp",EDGE,"E0"),sQuery(id+"F0.wireOp",EDGE,"E1")])],"isStart":true}),makeQuery(id+"F3.opExtrude","CAP_FACE",FACE,{"disambiguationData":[OSD([sQuery(id+"F2.wireOp",EDGE,"E2")])],"isStart":true})]}),makeQuery(id+"F7.opExtrude","CAP_FACE",FACE,{"disambiguationData":[OSD([sQuery(id+"F6.wireOp",EDGE,"E7"),sQuery(id+"F6.wireOp",EDGE,"E8"),sQuery(id+"F6.wireOp",EDGE,"E9"),sQuery(id+"F6.wireOp",EDGE,"E10")])],"isStart":true})]}),makeQuery(id+"F19.opExtrude","SWEPT_FACE",FACE,{"disambiguationData":[OSD([sQuery(id+"F18.wireOp",EDGE,"E31")])]})]});
            fillet(context, id + "F40", {"entities" : qUnion([Q0, Q1, Q2, Q3, Q4, Q5, Q6, Q7, Q8, Q9, Q10, Q11, Q12, Q13]), "radius" : 1.45 * mm, "tangentPropagation" : true, "allowEdgeOverflow" : false});
        }
    });
